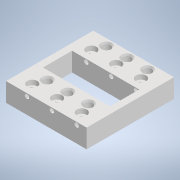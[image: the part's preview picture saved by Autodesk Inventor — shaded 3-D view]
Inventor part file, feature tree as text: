
AUTODESK INVENTOR PART (.ipt)
format: ipt  version: 2022 (Build 260153000, 153)  size: 670,208 bytes
history: native  units: mm
features: sketch x7, other x5, plane x3, pattern_linear x3, extrude x3, projected_geometry x3, loft x2, direct_edit x2, move_body x2, mirror x1, chamfer x1, sweep x1
ambient origin geometry x8: Origin, YZ Plane, XZ Plane, XY Plane, X Axis, Y Axis, Z Axis, Center Point
bodies: Solid1 (feature_tree)
feature tree (33):
  loft  "Loft1"
  plane  "Work Plane1"
  mirror  "Mirror1"
  loft  "Loft2"
  pattern_linear  "Rectangular Pattern1"  Count1=2 Spacing1=88.0mm
  chamfer  "Chamfer1"  Distance=2.0mm Angle=45.0deg
  sketch  "Sketch3"  dims[d8=0.0mm d9=90.0deg d10=20.0mm d12=88.0mm d13=2.0mm d14=2.0mm d15=45.0deg]
  extrude  "Extrusion1"  Depth=8.0mm
  other  "Work Point1"
  other  "Work Point2"
  plane  "Work Plane2"
  sweep  "Sweep1"
  pattern_linear  "Rectangular Pattern3"  Spacing1=0.0mm  [1 undecoded]
  direct_edit  "Direct Edit1"
  direct_edit  "Direct Edit2"
  plane  "Work Plane3"
  extrude  "Extrusion2"  Depth=10.0mm
  pattern_linear  "Rectangular Pattern4"  Spacing1=2.0mm  [1 undecoded]
  extrude  "Extrusion3"  TaperAngle=0.0deg  [1 undecoded]
  sketch  "Sketch1"  dims[d0=7.0mm d1=0.0mm d2=90.0deg d3=0.0mm d4=90.0deg]
  other  "Edges1"
  sketch  "Sketch2"  dims[d5=7.0mm d6=0.0mm d7=90.0deg]
  other  "Edges2"
  sketch  "Sketch5"  dims[d16=6.5mm d17=8.0mm]
  projected_geometry  "Projected Loop1"
  projected_geometry  "Projected Loop2"
  sketch  "Sketch6"  dims[d30=5.0mm d31=5.0mm]
  sketch  "Sketch7"  dims[d32=10.0mm]
  sketch  "Sketch8"  dims[d33=10.0mm d34=0.0mm d35=0.0mm d37=2.0mm d38=2.0mm d39=0.0mm d40=0.0mm d41=30.0mm d43=37.0mm d44=20.0mm d46=88.0mm d47=0.0mm d48=0.0mm d49=-2.0mm d50=0.0mm d51=0.0mm d52=3.0mm d53=29.0mm d54=12.0mm d55=0.0mm d56=20.0mm d58=88.0mm d59=30.0mm d61=37.0mm d62=2.0mm d63=0.0mm]
  projected_geometry  "Projected Loop3"
  other  "Cut-Extrude8"
  move_body  "Move1"
  move_body  "Move2"
note: 3 required parameter values undecoded (feature->parameter linkage not recoverable at this tier; creation-order binding heuristic only, values carry confidence <= 0.55)
